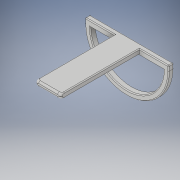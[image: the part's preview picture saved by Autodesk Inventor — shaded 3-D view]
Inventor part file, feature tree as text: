
AUTODESK INVENTOR PART (.ipt)
format: ipt  version: 2019 (Build 230136000, 136)  size: 203,776 bytes
history: native  units: mm
features: extrude x2, sketch x1, fillet x1
ambient origin geometry x8: Origin, YZ Plane, XZ Plane, XY Plane, X Axis, Y Axis, Z Axis, Center Point
bodies: Solid1 (feature_tree)
feature tree (4):
  sketch  "Sketch1"  dims[d0=30.0mm d1=6.0mm d2=100.0mm d3=0.0mm d4=100.0mm d5=6.0mm d6=1.0mm d7=6.0mm d8=0.0mm d9=2.0mm d10=1.0mm]
  extrude  "Extrusion1"  Depth=1.0mm
  extrude  "Extrusion2"  Depth=1.0mm TaperAngle=0.0deg
  fillet  "Fillet1"  Radius=100.0mm
